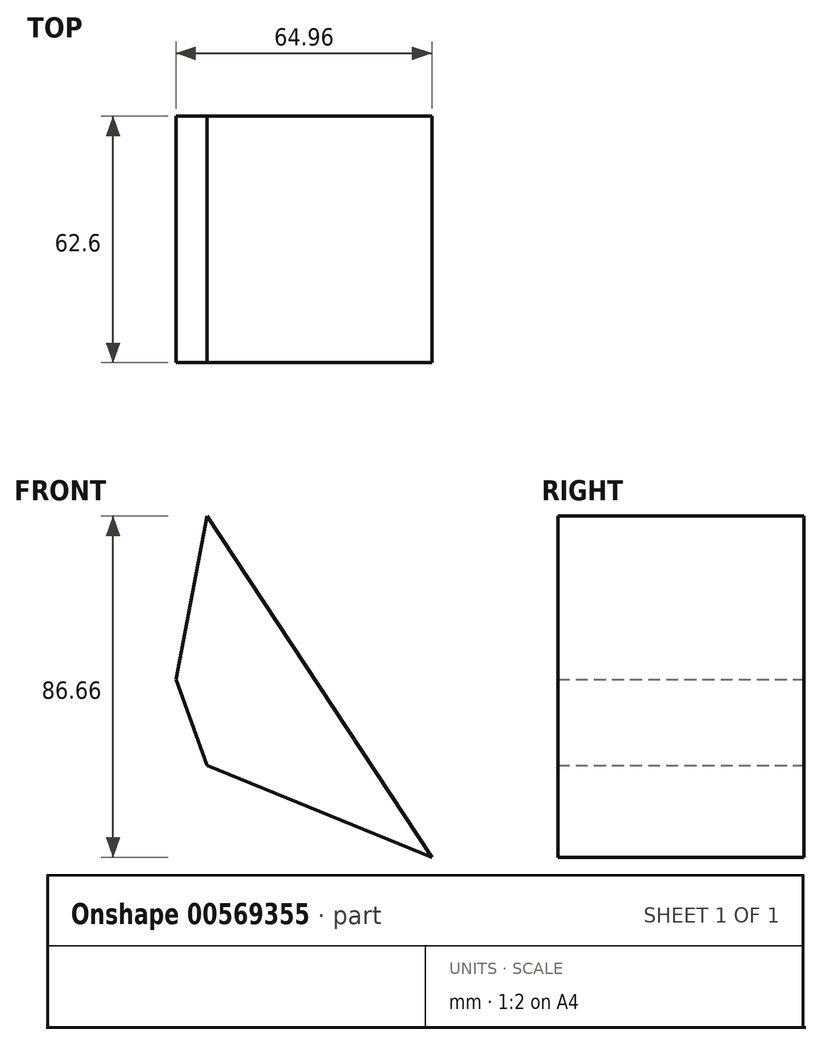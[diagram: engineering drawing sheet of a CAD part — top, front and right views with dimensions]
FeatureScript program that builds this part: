
annotation { "Feature Type Name" : "Feature", "Feature Type Description" : "" }
export const myFeature = defineFeature(function(context is Context, id is Id, definition is map)
    precondition{}
    {
        {
            var Q0;
            Q0=qCreatedBy(makeId("Front.planeOp"),FACE);
            var sketch = newSketch(context, id + "F0", { "sketchPlane" : qUnion([Q0])});
            skLineSegment(sketch, "E0", {"start": v(-57.08, 23.35) * mm, "end": v(0, 0) * mm});
            skLineSegment(sketch, "E1", {"start": v(0, 0) * mm, "end": v(-57.08, 86.66) * mm});
            skLineSegment(sketch, "E2", {"start": v(-57.08, 86.66) * mm, "end": v(-64.96, 45.16) * mm});
            skLineSegment(sketch, "E3", {"start": v(-64.96, 45.16) * mm, "end": v(-57.08, 23.35) * mm});
            skSolve(sketch);
        }
        {
            var Q0;
            Q0=makeQuery(id+"F0.imprint","IMPRINT",FACE,{"disambiguationData":[TD([[makeQuery(id+"F0.imprint","IMPRINT",EDGE,{"derivedFrom":sQuery(id+"F0.wireOp",EDGE,"E0")}),1.0]])]});
            extrude(context, id + "F1", {"entities" : qUnion([Q0]), "depth" : 62.6 * mm, "offsetDistance" : 25.4 * mm});
        }
    });
